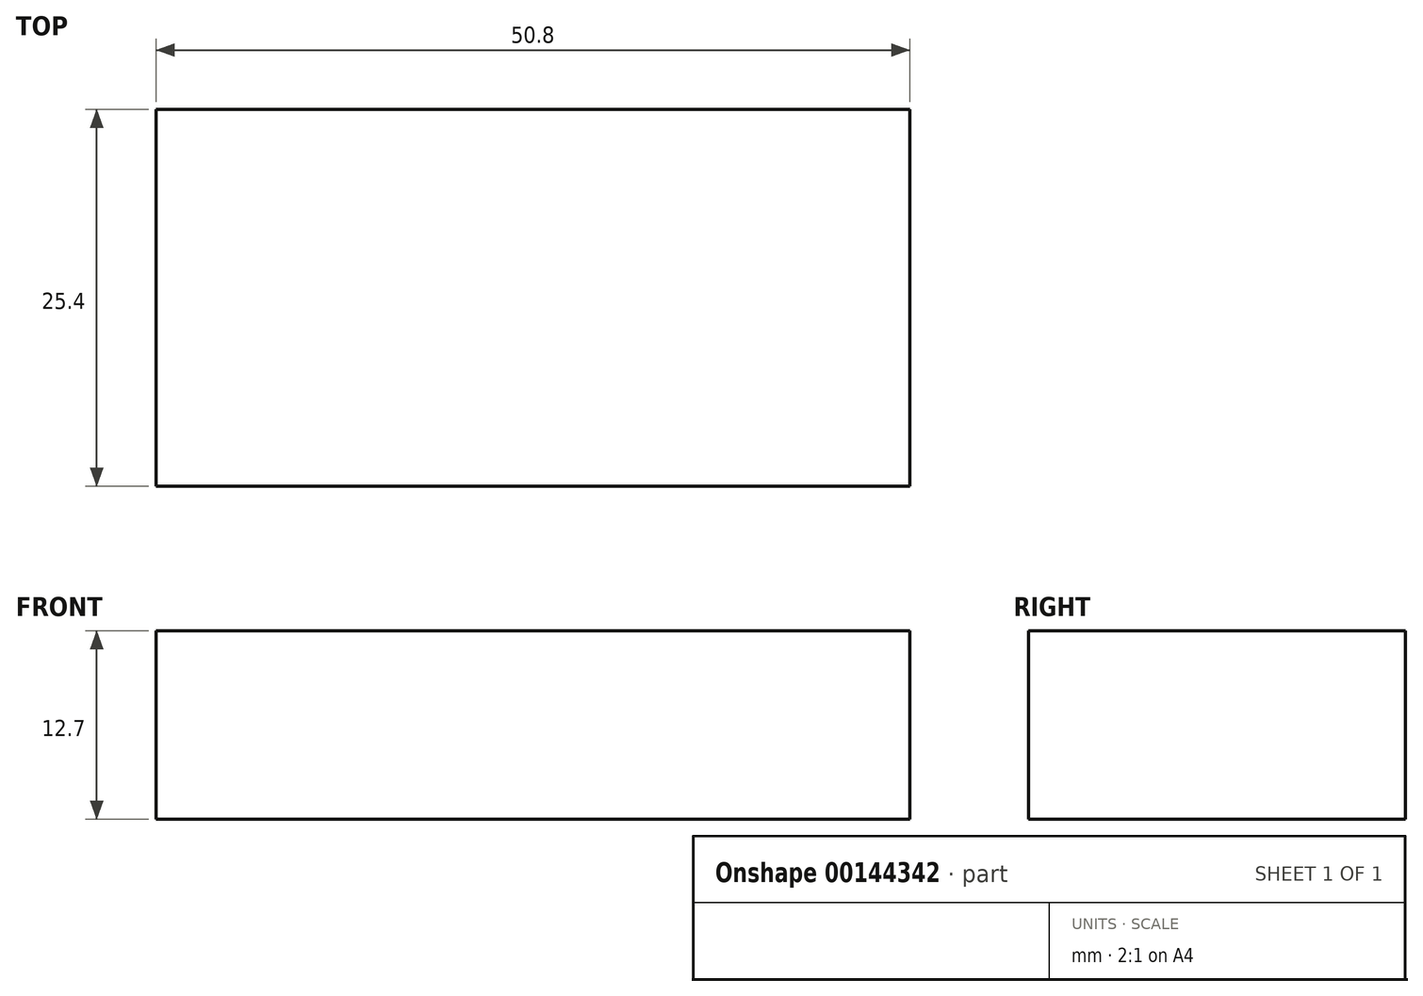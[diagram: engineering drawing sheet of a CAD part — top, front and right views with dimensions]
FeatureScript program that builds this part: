
annotation { "Feature Type Name" : "Feature", "Feature Type Description" : "" }
export const myFeature = defineFeature(function(context is Context, id is Id, definition is map)
    precondition{}
    {
        {
            var Q0;
            Q0=qCreatedBy(makeId("Top.planeOp"),FACE);
            var sketch = newSketch(context, id + "F0", { "sketchPlane" : qUnion([Q0])});
            skLineSegment(sketch, "E0.bottom", {"start": v(0, 0) * mm, "end": v(50.8, 0) * mm});
            skLineSegment(sketch, "E0.top", {"start": v(0, 25.4) * mm, "end": v(50.8, 25.4) * mm});
            skLineSegment(sketch, "E0.left", {"start": v(0, 0) * mm, "end": v(0, 25.4) * mm});
            skLineSegment(sketch, "E0.right", {"start": v(50.8, 0) * mm, "end": v(50.8, 25.4) * mm});
            skSolve(sketch);
        }
        {
            var Q0;
            Q0 = qSketchRegion(id + "F0", true);
            extrude(context, id + "F1", {"entities" : qUnion([Q0]), "depth" : 12.7 * mm});
        }
    });
